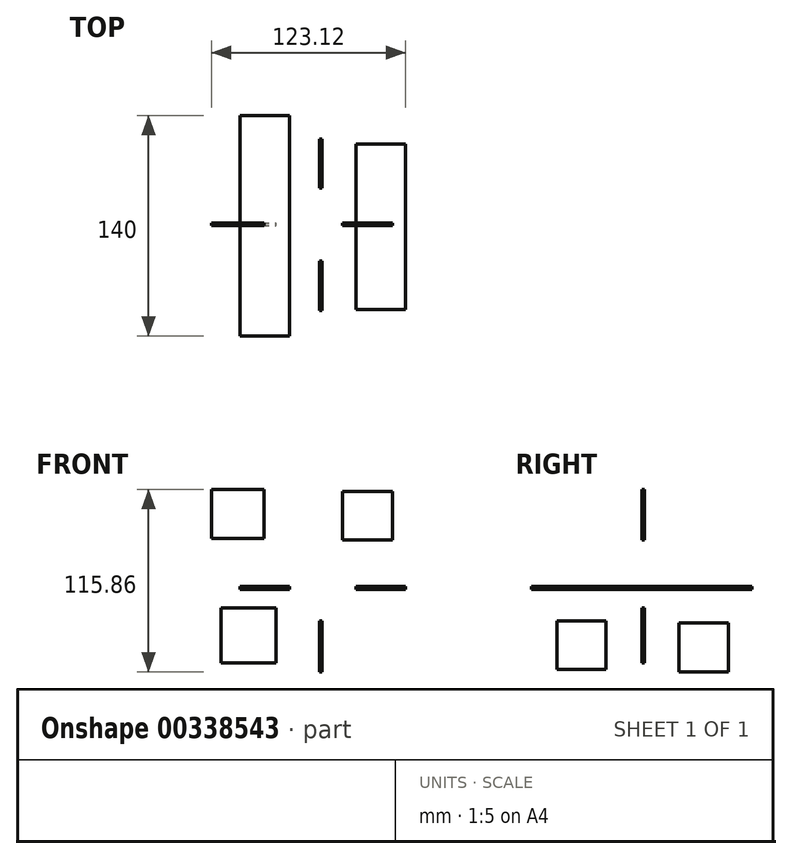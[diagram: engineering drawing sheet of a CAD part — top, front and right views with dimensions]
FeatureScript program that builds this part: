
annotation { "Feature Type Name" : "Feature", "Feature Type Description" : "" }
export const myFeature = defineFeature(function(context is Context, id is Id, definition is map)
    precondition{}
    {
        {
            var Q0;
            Q0=qCreatedBy(makeId("Top.planeOp"),FACE);
            var sketch = newSketch(context, id + "F0", { "sketchPlane" : qUnion([Q0])});
            skLineSegment(sketch, "E0.bottom", {"start": v(54.58, -54.95) * mm, "end": v(23.18, -54.95) * mm});
            skLineSegment(sketch, "E0.top", {"start": v(54.58, 50.05) * mm, "end": v(23.18, 50.05) * mm});
            skLineSegment(sketch, "E0.left", {"start": v(54.58, -54.95) * mm, "end": v(54.58, 50.05) * mm});
            skLineSegment(sketch, "E0.right", {"start": v(23.18, -54.95) * mm, "end": v(23.18, 50.05) * mm});
            skSolve(sketch);
        }
        {
            var Q0;
            Q0=makeQuery(id+"F0.imprint","IMPRINT",FACE,{"disambiguationData":[TD([[makeQuery(id+"F0.imprint","IMPRINT",EDGE,{"derivedFrom":sQuery(id+"F0.wireOp",EDGE,"E0.bottom")}),-1.0]])]});
            extrude(context, id + "F1", {"entities" : qUnion([Q0]), "depth" : 2 * mm});
        }
        {
            var Q0;
            Q0=qCreatedBy(makeId("Top.planeOp"),FACE);
            var sketch = newSketch(context, id + "F2", { "sketchPlane" : qUnion([Q0])});
            skLineSegment(sketch, "E1.bottom", {"start": v(-19.07, -71.78) * mm, "end": v(-50.47, -71.78) * mm});
            skLineSegment(sketch, "E1.top", {"start": v(-19.07, 68.22) * mm, "end": v(-50.47, 68.22) * mm});
            skLineSegment(sketch, "E1.left", {"start": v(-19.07, -71.78) * mm, "end": v(-19.07, 68.22) * mm});
            skLineSegment(sketch, "E1.right", {"start": v(-50.47, -71.78) * mm, "end": v(-50.47, 68.22) * mm});
            skSolve(sketch);
        }
        {
            var Q0;
            Q0=makeQuery(id+"F2.imprint","IMPRINT",FACE,{"disambiguationData":[TD([[makeQuery(id+"F2.imprint","IMPRINT",EDGE,{"derivedFrom":sQuery(id+"F2.wireOp",EDGE,"E1.bottom")}),-1.0]])]});
            extrude(context, id + "F3", {"entities" : qUnion([Q0]), "depth" : 2 * mm});
        }
        {
            var Q0;
            Q0=qCreatedBy(makeId("Front.planeOp"),FACE);
            var sketch = newSketch(context, id + "F4", { "sketchPlane" : qUnion([Q0])});
            skLineSegment(sketch, "E2.bottom", {"start": v(-68.54, 63.52) * mm, "end": v(-35.14, 63.52) * mm});
            skLineSegment(sketch, "E2.top", {"start": v(-68.54, 32.52) * mm, "end": v(-35.14, 32.52) * mm});
            skLineSegment(sketch, "E2.left", {"start": v(-68.54, 63.52) * mm, "end": v(-68.54, 32.52) * mm});
            skLineSegment(sketch, "E2.right", {"start": v(-35.14, 63.52) * mm, "end": v(-35.14, 32.52) * mm});
            skSolve(sketch);
        }
        {
            var Q0;
            Q0=makeQuery(id+"F4.imprint","IMPRINT",FACE,{"disambiguationData":[TD([[makeQuery(id+"F4.imprint","IMPRINT",EDGE,{"derivedFrom":sQuery(id+"F4.wireOp",EDGE,"E2.bottom")}),-1.0]])]});
            extrude(context, id + "F5", {"entities" : qUnion([Q0]), "depth" : 1.6 * mm});
        }
        {
            var Q0;
            Q0=qCreatedBy(makeId("Front.planeOp"),FACE);
            var sketch = newSketch(context, id + "F6", { "sketchPlane" : qUnion([Q0])});
            skLineSegment(sketch, "E3.bottom", {"start": v(14.56, 62.4) * mm, "end": v(46.36, 62.4) * mm});
            skLineSegment(sketch, "E3.top", {"start": v(14.56, 31.4) * mm, "end": v(46.36, 31.4) * mm});
            skLineSegment(sketch, "E3.left", {"start": v(14.56, 62.4) * mm, "end": v(14.56, 31.4) * mm});
            skLineSegment(sketch, "E3.right", {"start": v(46.36, 62.4) * mm, "end": v(46.36, 31.4) * mm});
            skSolve(sketch);
        }
        {
            var Q0;
            Q0=makeQuery(id+"F6.imprint","IMPRINT",FACE,{"disambiguationData":[TD([[makeQuery(id+"F6.imprint","IMPRINT",EDGE,{"derivedFrom":sQuery(id+"F6.wireOp",EDGE,"E3.bottom")}),-1.0]])]});
            extrude(context, id + "F7", {"entities" : qUnion([Q0]), "depth" : 1.6 * mm});
        }
        {
            var Q0;
            Q0=qCreatedBy(makeId("Right.planeOp"),FACE);
            var sketch = newSketch(context, id + "F8", { "sketchPlane" : qUnion([Q0])});
            skLineSegment(sketch, "E4.bottom", {"start": v(-55.7, -19.84) * mm, "end": v(-24.3, -19.84) * mm});
            skLineSegment(sketch, "E4.top", {"start": v(-55.7, -50.84) * mm, "end": v(-24.3, -50.84) * mm});
            skLineSegment(sketch, "E4.left", {"start": v(-55.7, -19.84) * mm, "end": v(-55.7, -50.84) * mm});
            skLineSegment(sketch, "E4.right", {"start": v(-24.3, -19.84) * mm, "end": v(-24.3, -50.84) * mm});
            skSolve(sketch);
        }
        {
            var Q0;
            Q0=qCreatedBy(makeId("Right.planeOp"),FACE);
            var sketch = newSketch(context, id + "F9", { "sketchPlane" : qUnion([Q0])});
            skLineSegment(sketch, "E5.bottom", {"start": v(22.06, -21.34) * mm, "end": v(53.46, -21.34) * mm});
            skLineSegment(sketch, "E5.top", {"start": v(22.06, -52.34) * mm, "end": v(53.46, -52.34) * mm});
            skLineSegment(sketch, "E5.left", {"start": v(22.06, -21.34) * mm, "end": v(22.06, -52.34) * mm});
            skLineSegment(sketch, "E5.right", {"start": v(53.46, -21.34) * mm, "end": v(53.46, -52.34) * mm});
            skSolve(sketch);
        }
        {
            var Q0;
            Q0=makeQuery(id+"F8.imprint","IMPRINT",FACE,{"disambiguationData":[TD([[makeQuery(id+"F8.imprint","IMPRINT",EDGE,{"derivedFrom":sQuery(id+"F8.wireOp",EDGE,"E4.bottom")}),-1.0]])]});
            extrude(context, id + "F10", {"entities" : qUnion([Q0]), "depth" : 1.6 * mm});
        }
        {
            var Q0;
            Q0=makeQuery(id+"F9.imprint","IMPRINT",FACE,{"disambiguationData":[TD([[makeQuery(id+"F9.imprint","IMPRINT",EDGE,{"derivedFrom":sQuery(id+"F9.wireOp",EDGE,"E5.bottom")}),-1.0]])]});
            extrude(context, id + "F11", {"entities" : qUnion([Q0]), "depth" : 1.6 * mm});
        }
        {
            var Q0;
            Q0=qCreatedBy(makeId("Front.planeOp"),FACE);
            var sketch = newSketch(context, id + "F12", { "sketchPlane" : qUnion([Q0])});
            skLineSegment(sketch, "E6.bottom", {"start": v(-62.66, -11.73) * mm, "end": v(-27.66, -11.73) * mm});
            skLineSegment(sketch, "E6.top", {"start": v(-62.66, -46.73) * mm, "end": v(-27.66, -46.73) * mm});
            skLineSegment(sketch, "E6.left", {"start": v(-62.66, -11.73) * mm, "end": v(-62.66, -46.73) * mm});
            skLineSegment(sketch, "E6.right", {"start": v(-27.66, -11.73) * mm, "end": v(-27.66, -46.73) * mm});
            skSolve(sketch);
        }
        {
            var Q0;
            Q0=makeQuery(id+"F12.imprint","IMPRINT",FACE,{"disambiguationData":[TD([[makeQuery(id+"F12.imprint","IMPRINT",EDGE,{"derivedFrom":sQuery(id+"F12.wireOp",EDGE,"E6.bottom")}),-1.0]])]});
            extrude(context, id + "F13", {"entities" : qUnion([Q0]), "depth" : 1.6 * mm});
        }
    });
